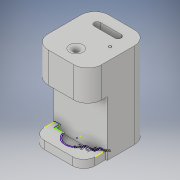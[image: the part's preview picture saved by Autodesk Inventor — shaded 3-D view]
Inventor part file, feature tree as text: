
AUTODESK INVENTOR PART (.ipt)
format: ipt  version: 2017 (Build 210142000, 142)  size: 360,448 bytes
history: native  units: in
note: dims shown in document units (in); Inventor stores cm internally (conversion verified against a paired STEP export)
features: extrude x14, sketch x14, other x3
ambient origin geometry x8: Origin, YZ Plane, XZ Plane, XY Plane, X Axis, Y Axis, Z Axis, Center Point
bodies: body (feature_tree)
feature tree (31):
  extrude  "bace bottom"  Depth=0.2457in
  extrude  "sharpener top"  Depth=0.0828in
  other  "sharpener hole"
  extrude  "Extrusion of sharpener hole"  TaperAngle=90.0deg  [1 undecoded]
  extrude  "pencil holder"  Depth=0.0545in TaperAngle=0.0deg
  extrude  "pencil holder bottom"  Depth=0.0408in TaperAngle=0.0deg
  extrude  "sharpened light hole"  Depth=0.0081in
  extrude  "sharpened light indicator"  Depth=0.0081in
  extrude  "bottom of bace"  Depth=0.0067in
  extrude  "cut for holder"  Depth=0.0042in
  extrude  "bottom of tray slot"  Depth=0.0373in
  sketch  "Sketch15"  dims[d44=0.0641in d45=0.0373in]
  extrude  "nobes for connection"  Depth=0.0155in
  extrude  "connection to nobes"  Depth=0.0108in
  extrude  "Extrusion15"  Depth=0.0625in
  sketch  "Sketch19"  dims[d55=0.0625in d56=0.0in d57=0.0133in d59=0.0266in d60=0.0133in d61=0.0625in d62=0.0in d63=0.008in d64=0.0in d66=0.0705in d67=0.0in d68=0.018in d69=0.0052in d70=0.0243in d71=0.0in d74=0.008in d75=0.0in d76=0.0349in d77=0.0314in d78=0.0523in d79=0.0038in d80=0.0064in d81=0.0in d86=0.0062in d87=0.0062in d88=0.0062in d89=0.0062in]
  extrude  "container for wasts"  Depth=0.0062in
  sketch  "Sketch17"  dims[d50=0.0769in d51=0.0108in]
  sketch  "Sketch3"  dims[d7=0.288in d8=0.0in d9=0.2457in]
  sketch  "Sketch6"  dims[d11=0.1593in d12=0.0828in]
  sketch  "Sketch7"  dims[d13=0.1819in d14=0.0in d16=90.0deg]
  sketch  "Sketch8"  dims[d17=0.0625in d18=0.0in d19=0.0545in d20=0.0in]
  sketch  "Sketch9"  dims[d22=0.0625in d23=0.0in d25=0.0408in d26=0.0in]
  sketch  "Sketch10"  dims[d29=0.0081in d30=0.0081in]
  sketch  "Sketch12"  dims[d31=0.0081in d32=0.0081in]
  sketch  "Sketch13"  dims[d33=0.0067in d34=0.0509in]
  other  "light indicator"
  sketch  "Sketch14"  dims[d37=0.0794in d39=0.0042in]
  other  "container"
  sketch  "Sketch16"  dims[d47=0.1616in d48=0.0155in]
  sketch  "Sketch18"  dims[d52=0.0625in d53=0.0in d54=0.0127in]
note: 1 required parameter value undecoded (feature->parameter linkage not recoverable at this tier; creation-order binding heuristic only, values carry confidence <= 0.55)
